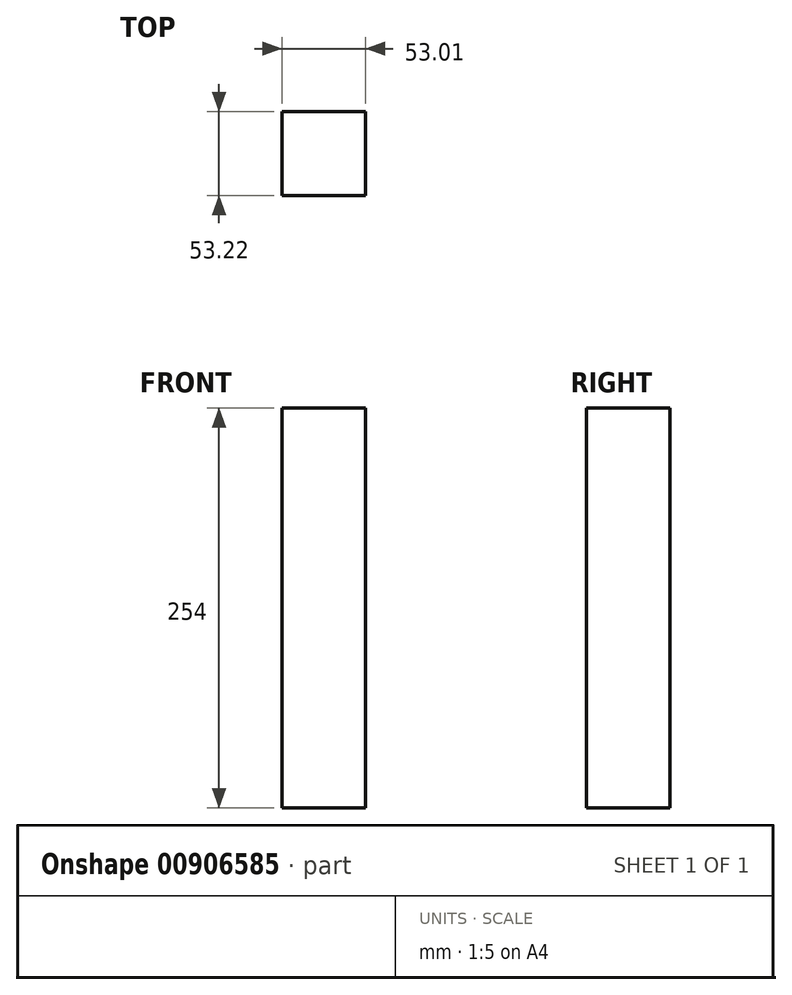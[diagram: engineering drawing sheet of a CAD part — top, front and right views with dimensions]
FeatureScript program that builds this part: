
annotation { "Feature Type Name" : "Feature", "Feature Type Description" : "" }
export const myFeature = defineFeature(function(context is Context, id is Id, definition is map)
    precondition{}
    {
        {
            var Q0;
            Q0=qCreatedBy(makeId("Top.planeOp"),FACE);
            var sketch = newSketch(context, id + "F0", { "sketchPlane" : qUnion([Q0])});
            skLineSegment(sketch, "E0.bottom", {"start": v(-20.63, 23.94) * mm, "end": v(32.38, 23.94) * mm});
            skLineSegment(sketch, "E0.top", {"start": v(-20.63, -29.28) * mm, "end": v(32.38, -29.28) * mm});
            skLineSegment(sketch, "E0.left", {"start": v(-20.63, 23.94) * mm, "end": v(-20.63, -29.28) * mm});
            skLineSegment(sketch, "E0.right", {"start": v(32.38, 23.94) * mm, "end": v(32.38, -29.28) * mm});
            skSolve(sketch);
        }
        {
            var Q0;
            Q0=makeQuery(id+"F0.imprint","IMPRINT",FACE,{"disambiguationData":[TD([[makeQuery(id+"F0.imprint","IMPRINT",EDGE,{"derivedFrom":sQuery(id+"F0.wireOp",EDGE,"E0.bottom")}),-1.0]])]});
            extrude(context, id + "F1", {"entities" : qUnion([Q0]), "depth" : 254 * mm, "offsetDistance" : 25.4 * mm});
        }
    });
